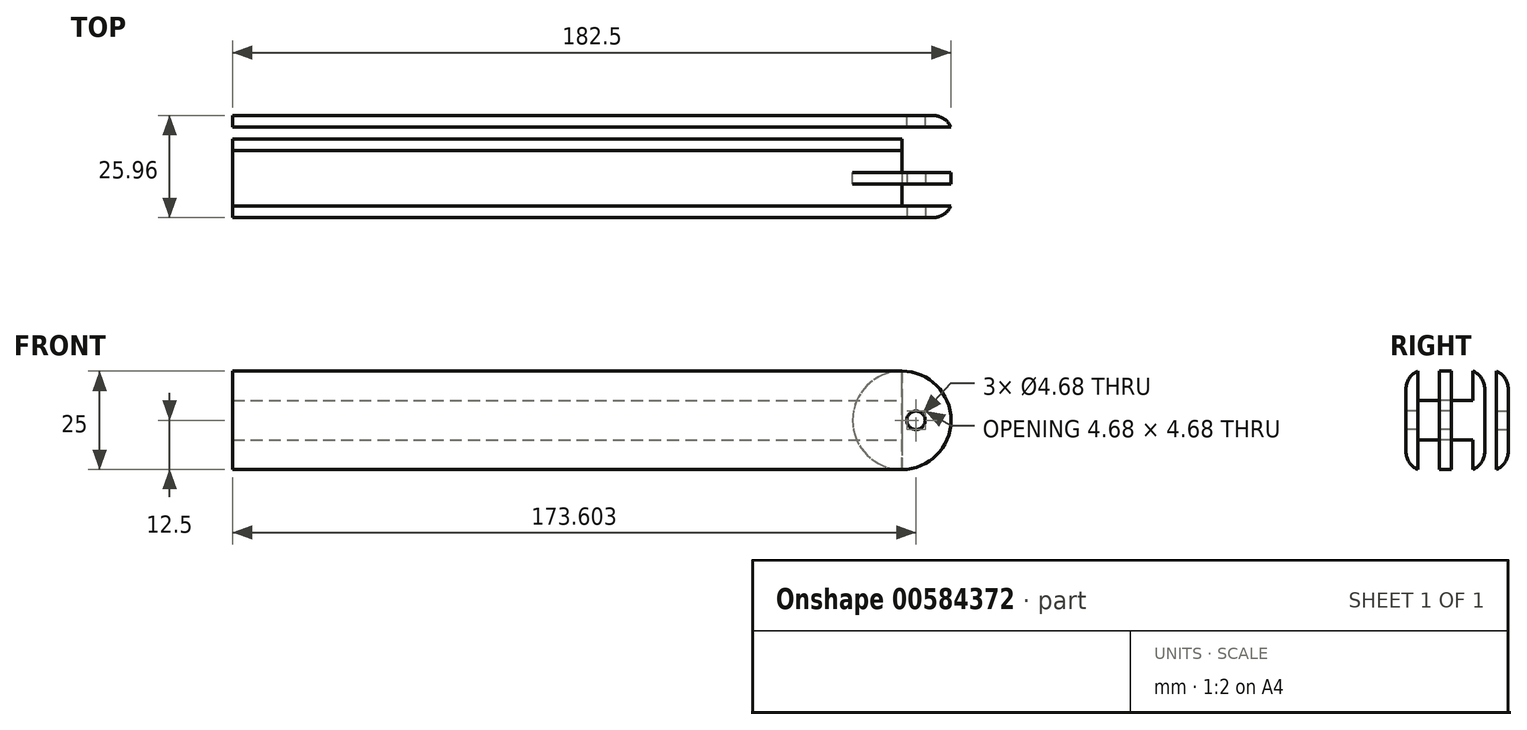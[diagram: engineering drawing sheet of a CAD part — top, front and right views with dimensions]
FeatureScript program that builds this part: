
annotation { "Feature Type Name" : "Feature", "Feature Type Description" : "" }
export const myFeature = defineFeature(function(context is Context, id is Id, definition is map)
    precondition{}
    {
        {
            var Q0;
            Q0=qCreatedBy(makeId("Top.planeOp"),FACE);
            var sketch = newSketch(context, id + "F0", { "sketchPlane" : qUnion([Q0])});
            skLineSegment(sketch, "E0.bottom", {"start": v(-85, 7.02) * mm, "end": v(85, 7.02) * mm});
            skLineSegment(sketch, "E0.top", {"start": v(-85, -12.98) * mm, "end": v(85, -12.98) * mm});
            skLineSegment(sketch, "E0.left", {"start": v(-85, 7.02) * mm, "end": v(-85, -12.98) * mm});
            skLineSegment(sketch, "E0.right", {"start": v(85, 7.02) * mm, "end": v(85, -12.98) * mm});
            skPoint(sketch, "E0.middle", {"position": v(0, -2.98) * mm});
            skLineSegment(sketch, "E1", {"start": v(85, 4.02) * mm, "end": v(-85, 4.02) * mm});
            skLineSegment(sketch, "E2", {"start": v(-85, -9.98) * mm, "end": v(85, -9.98) * mm});
            skSolve(sketch);
        }
        {
            var Q0;
            {var subQ0=sQuery(id+"F0.wireOp",EDGE,"E0.top");Q0=makeQuery(id+"F0.imprint","IMPRINT",FACE,{"disambiguationData":[TD([[makeQuery(id+"F0.imprint","IMPRINT",EDGE,{"derivedFrom":subQ0}),1.0]])]});}
            extrude(context, id + "F1", {"entities" : qUnion([Q0]), "endBound" : BoundingType.SYMMETRIC, "depth" : 25 * mm, "offsetDistance" : 25 * mm});
        }
        {
            var Q0;
            Q0 = qSketchRegion(id + "F1a5bLgjiLIVfdd_2", true);
            var Q1;
            {var subQ0=sQuery(id+"F0.wireOp",EDGE,"E1");Q1=makeQuery(id+"F0.imprint","IMPRINT",FACE,{"disambiguationData":[TD([[makeQuery(id+"F0.imprint","IMPRINT",EDGE,{"derivedFrom":subQ0}),1.0]])]});}
            extrude(context, id + "F2", {"entities" : qUnion([Q0, Q1]), "endBound" : BoundingType.SYMMETRIC, "depth" : 10 * mm, "offsetDistance" : 25 * mm});
        }
        {
            var Q0;
            {var subQ0=sQuery(id+"F0.wireOp",EDGE,"E0.bottom");Q0=makeQuery(id+"F0.imprint","IMPRINT",FACE,{"disambiguationData":[TD([[makeQuery(id+"F0.imprint","IMPRINT",EDGE,{"derivedFrom":subQ0}),-1.0]])]});}
            extrude(context, id + "F3", {"entities" : qUnion([Q0]), "operationType" : NewBodyOperationType.ADD, "endBound" : BoundingType.SYMMETRIC, "depth" : 25 * mm, "offsetDistance" : 25 * mm});
        }
        {
            var Q0;
            Q0=makeQuery(id+"F1.opExtrude","CAP_EDGE",EDGE,{"disambiguationData":[OSD([sQuery(id+"F0.wireOp",EDGE,"E0.top")])],"isStart":true});
            var Q1;
            Q1=makeQuery(id+"F1.opExtrude","CAP_EDGE",EDGE,{"disambiguationData":[OSD([sQuery(id+"F0.wireOp",EDGE,"E0.top")])],"isStart":false});
            var Q2;
            Q2=makeQuery(id+"F3.opExtrude","CAP_EDGE",EDGE,{"disambiguationData":[OSD([sQuery(id+"F0.wireOp",EDGE,"E0.bottom")])],"isStart":true});
            var Q3;
            Q3=makeQuery(id+"F3.opExtrude","CAP_EDGE",EDGE,{"disambiguationData":[OSD([sQuery(id+"F0.wireOp",EDGE,"E0.bottom")])],"isStart":false});
            fillet(context, id + "F4", {"entities" : qUnion([Q0, Q1, Q2, Q3]), "radius" : 5 * mm, "tangentPropagation" : true, "allowEdgeOverflow" : false});
        }
        {
            var Q0;
            {var subQ0=sQuery(id+"F0.wireOp",EDGE,"E0.right");Q0=makeQuery(id+"F1.opExtrude","SWEPT_FACE",FACE,{"disambiguationData":[OSD([subQ0]),TDD([makeQuery(id+"F0.imprint","IMPRINT",EDGE,{"disambiguationData":[TD([[makeQuery(id+"F0.imprint","INTERSECT",VERTEX,{"derivedFrom":[sQuery(id+"F0.wireOp",EDGE,"E0.bottom"),subQ0]}),-1.0]])],"derivedFrom":subQ0})])]});}
            var sketch = newSketch(context, id + "F5", { "sketchPlane" : qUnion([Q0])});
            skPoint(sketch, "E3", {"position": v(-2.98, 0) * mm});
            skPoint(sketch, "E4", {"position": v(-1.48, 0) * mm});
            skLineSegment(sketch, "E5", {"start": v(0, 0) * mm, "end": v(0, 0) * mm});
            skLineSegment(sketch, "E6.bottom", {"start": v(-1.48, 0) * mm, "end": v(-2.98, 0) * mm});
            skLineSegment(sketch, "E6.top", {"start": v(-1.48, 12.5) * mm, "end": v(-2.98, 12.5) * mm});
            skLineSegment(sketch, "E6.left", {"start": v(-1.48, 0) * mm, "end": v(-1.48, 12.5) * mm});
            skLineSegment(sketch, "E6.right", {"start": v(-2.98, 0) * mm, "end": v(-2.98, 12.5) * mm});
            skLineSegment(sketch, "E7.top", {"start": v(-1.48, -12.5) * mm, "end": v(-2.98, -12.5) * mm});
            skLineSegment(sketch, "E7.left", {"start": v(-1.48, 0) * mm, "end": v(-1.48, -12.5) * mm});
            skLineSegment(sketch, "E7.right", {"start": v(-2.98, 0) * mm, "end": v(-2.98, -12.5) * mm});
            skLineSegment(sketch, "E8.bottom", {"start": v(-2.98, 0) * mm, "end": v(-4.48, 0) * mm});
            skLineSegment(sketch, "E8.top", {"start": v(-2.98, 12.5) * mm, "end": v(-4.48, 12.5) * mm});
            skLineSegment(sketch, "E8.right", {"start": v(-4.48, 0) * mm, "end": v(-4.48, 12.5) * mm});
            skLineSegment(sketch, "E9.top", {"start": v(-2.98, -12.5) * mm, "end": v(-4.48, -12.5) * mm});
            skLineSegment(sketch, "E9.right", {"start": v(-4.48, 0) * mm, "end": v(-4.48, -12.5) * mm});
            skLineSegment(sketch, "E10.bottom", {"start": v(7.02, 12.5) * mm, "end": v(-12.98, 12.5) * mm});
            skLineSegment(sketch, "E10.top", {"start": v(7.02, -12.5) * mm, "end": v(-12.98, -12.5) * mm});
            skLineSegment(sketch, "E10.left", {"start": v(7.02, 12.5) * mm, "end": v(7.02, -12.5) * mm});
            skLineSegment(sketch, "E10.right", {"start": v(-12.98, 12.5) * mm, "end": v(-12.98, -12.5) * mm});
            skLineSegment(sketch, "E11.top", {"start": v(7.02, 0) * mm, "end": v(-9.98, 0) * mm});
            skLineSegment(sketch, "E11.left", {"start": v(7.02, 12.5) * mm, "end": v(7.02, 0) * mm});
            skLineSegment(sketch, "E11.right", {"start": v(-9.98, 12.5) * mm, "end": v(-9.98, 0) * mm});
            skLineSegment(sketch, "E12.top", {"start": v(7.02, -12.5) * mm, "end": v(-9.98, -12.5) * mm});
            skLineSegment(sketch, "E12.left", {"start": v(7.02, 0) * mm, "end": v(7.02, -12.5) * mm});
            skLineSegment(sketch, "E12.right", {"start": v(-9.98, 0) * mm, "end": v(-9.98, -12.5) * mm});
            skLineSegment(sketch, "E13", {"start": v(-12.64, 0) * mm, "end": v(-12.98, 0) * mm});
            skLineSegment(sketch, "E14.bottom", {"start": v(-12.98, 0) * mm, "end": v(-9.99, 0) * mm});
            skLineSegment(sketch, "E14.top", {"start": v(-12.98, 12.5) * mm, "end": v(-9.99, 12.5) * mm});
            skLineSegment(sketch, "E14.left", {"start": v(-12.98, 0) * mm, "end": v(-12.98, 12.5) * mm});
            skLineSegment(sketch, "E14.right", {"start": v(-9.99, 0) * mm, "end": v(-9.99, 12.5) * mm});
            skLineSegment(sketch, "E15.top", {"start": v(-12.98, -12.5) * mm, "end": v(-9.99, -12.5) * mm});
            skLineSegment(sketch, "E15.left", {"start": v(-12.98, 0) * mm, "end": v(-12.98, -12.5) * mm});
            skLineSegment(sketch, "E15.right", {"start": v(-9.99, 0) * mm, "end": v(-9.99, -12.5) * mm});
            skLineSegment(sketch, "E16.bottom", {"start": v(7.02, 12.5) * mm, "end": v(4.03, 12.5) * mm});
            skLineSegment(sketch, "E16.top", {"start": v(7.02, 0) * mm, "end": v(4.03, 0) * mm});
            skLineSegment(sketch, "E16.right", {"start": v(4.03, 12.5) * mm, "end": v(4.03, 0) * mm});
            skLineSegment(sketch, "E17.top", {"start": v(7.02, -12.5) * mm, "end": v(4.03, -12.5) * mm});
            skLineSegment(sketch, "E17.right", {"start": v(4.03, 0) * mm, "end": v(4.03, -12.5) * mm});
            skSolve(sketch);
        }
        {
            var Q0;
            {var subQ0=sQuery(id+"F5.wireOp",EDGE,"E14.bottom");var subQ3=makeQuery(id+"F5.imprint","IMPRINT",VERTEX,{"derivedFrom":subQ0});Q0=makeQuery(id+"F5.imprint","IMPRINT",FACE,{"disambiguationData":[TD([[makeQuery(id+"F5.imprint","IMPRINT",EDGE,{"disambiguationData":[TD([[subQ3,1.0]])],"derivedFrom":subQ0}),1.0]])]});}
            var Q1;
            Q1=makeQuery(id+"F5.imprint","IMPRINT",FACE,{"disambiguationData":[TD([[makeQuery(id+"F5.imprint","IMPRINT",EDGE,{"derivedFrom":sQuery(id+"F5.wireOp",EDGE,"E16.bottom")}),1.0]])]});
            var Q2;
            Q2=sQuery(id+"F0.wireOp",EDGE,"E0.right");
            revolve(context, id + "F6", {"operationType" : NewBodyOperationType.ADD, "entities" : qUnion([Q0, Q1]), "axis" : qUnion([Q2]), "revolveType" : RevolveType.FULL});
        }
        {
            var Q0;
            {var subQ0=sQuery(id+"F5.wireOp",EDGE,"E6.left");Q0=makeQuery(id+"F5.imprint","IMPRINT",FACE,{"disambiguationData":[TD([[makeQuery(id+"F5.imprint","IMPRINT",EDGE,{"derivedFrom":subQ0}),1.0]])]});}
            var Q1;
            {var subQ0=sQuery(id+"F5.wireOp",EDGE,"E6.right");Q1=makeQuery(id+"F5.imprint","IMPRINT",FACE,{"disambiguationData":[TD([[makeQuery(id+"F5.imprint","IMPRINT",EDGE,{"derivedFrom":subQ0}),1.0]])]});}
            var Q2;
            Q2=sQuery(id+"F0.wireOp",EDGE,"E0.right");
            revolve(context, id + "F7", {"entities" : qUnion([Q0, Q1]), "axis" : qUnion([Q2]), "revolveType" : RevolveType.FULL});
        }
        {
            var Q0;
            Q0=makeQuery(id+"F6.boolean.opBoolean","MERGE",FACE,{"derivedFrom":[makeQuery(id+"F1.opExtrude","SWEPT_FACE",FACE,{"disambiguationData":[OSD([sQuery(id+"F0.wireOp",EDGE,"E0.top")])]}),makeQuery(id+"F6.opRevolve","SWEPT_FACE",FACE,{"disambiguationData":[OSD([sQuery(id+"F5.wireOp",EDGE,"E14.left")])]})]});
            var sketch = newSketch(context, id + "F8", { "sketchPlane" : qUnion([Q0])});
            skCircle(sketch, "E18", {"center": v(88.6, 0) * mm, "radius": 2.34 * mm});
            skPoint(sketch, "E18.centerSnap0", {"position": v(92.92, 0) * mm});
            skSolve(sketch);
        }
        {
            var Q0;
            Q0=makeQuery(id+"F8.imprint","IMPRINT",FACE,{"disambiguationData":[TD([[makeQuery(id+"F8.imprint","IMPRINT",EDGE,{"derivedFrom":sQuery(id+"F8.wireOp",EDGE,"E18")}),1.0]])]});
            extrude(context, id + "F9", {"entities" : qUnion([Q0]), "operationType" : NewBodyOperationType.REMOVE, "endBound" : BoundingType.THROUGH_ALL, "oppositeDirection" : true, "depth" : 25 * mm, "offsetDistance" : 25 * mm});
        }
        {
            var Q0;
            Q0=makeQuery(id+"F1.opExtrude","SWEPT_BODY",BODY,{"disambiguationData":[OSD([sQuery(id+"F0.wireOp",EDGE,"E0.top"),sQuery(id+"F0.wireOp",EDGE,"E0.left"),sQuery(id+"F0.wireOp",EDGE,"E0.right"),sQuery(id+"F0.wireOp",EDGE,"E2")])]});
            var Q1;
            Q1=qCreatedBy(makeId("Front.planeOp"),FACE);
            mirror(context, id + "F10", {"entities" : qUnion([Q0]), "mirrorPlane" : qUnion([Q1])});
        }
    });
